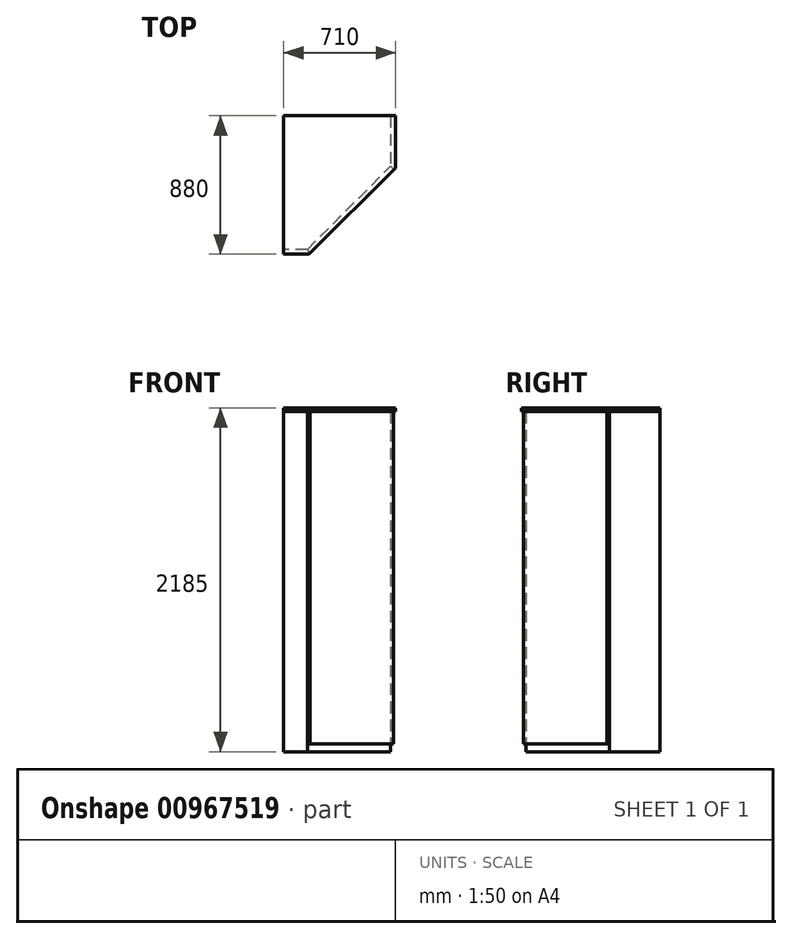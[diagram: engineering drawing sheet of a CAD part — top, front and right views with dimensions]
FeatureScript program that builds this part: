
annotation { "Feature Type Name" : "Feature", "Feature Type Description" : "" }
export const myFeature = defineFeature(function(context is Context, id is Id, definition is map)
    precondition{}
    {
        {
            assignVariable(context, id + "F0", {"variableType" : VariableType.LENGTH, "name" : "H", "lengthValue" : 2200 * mm});
        }
        {
            var Q0;
            Q0=qCreatedBy(makeId("Top.planeOp"),FACE);
            var sketch = newSketch(context, id + "F1", { "sketchPlane" : qUnion([Q0])});
            skLineSegment(sketch, "E0", {"start": v(0, 0) * mm, "end": v(680, 0) * mm});
            skLineSegment(sketch, "E1", {"start": v(680, 0) * mm, "end": v(680, -320) * mm});
            skLineSegment(sketch, "E2", {"start": v(680, -320) * mm, "end": v(150, -850) * mm});
            skLineSegment(sketch, "E3", {"start": v(150, -850) * mm, "end": v(0, -850) * mm});
            skLineSegment(sketch, "E4", {"start": v(0, -850) * mm, "end": v(0, 0) * mm});
            skSolve(sketch);
        }
        {
            var Q0;
            Q0 = qSketchRegion(id + "F1", true);
            extrude(context, id + "F2", {"entities" : qUnion([Q0]), "depth" : getVariable(context, 'H') - 40 * mm, "offsetDistance" : 25 * mm});
        }
        {
            var Q0;
            Q0=makeQuery(id+"F2.opExtrude","SWEPT_FACE",FACE,{"disambiguationData":[OSD([sQuery(id+"F1.wireOp",EDGE,"E2")])]});
            var sketch = newSketch(context, id + "F3", { "sketchPlane" : qUnion([Q0])});
            skLineSegment(sketch, "E5.bottom", {"start": v(-494.97, 2160) * mm, "end": v(254.56, 2160) * mm});
            skLineSegment(sketch, "E5.top", {"start": v(-494.97, 50) * mm, "end": v(254.56, 50) * mm});
            skLineSegment(sketch, "E5.left", {"start": v(-494.97, 2160) * mm, "end": v(-494.97, 50) * mm});
            skLineSegment(sketch, "E5.right", {"start": v(254.56, 2160) * mm, "end": v(254.56, 50) * mm});
            skSolve(sketch);
        }
        {
            var Q0;
            Q0 = qSketchRegion(id + "F3", true);
            extrude(context, id + "F4", {"entities" : qUnion([Q0]), "depth" : 25 * mm, "offsetDistance" : 25 * mm});
        }
        {
            var Q0;
            Q0=makeQuery(id+"F2.opExtrude","CAP_FACE",FACE,{"disambiguationData":[OSD([sQuery(id+"F1.wireOp",EDGE,"E0"),sQuery(id+"F1.wireOp",EDGE,"E1"),sQuery(id+"F1.wireOp",EDGE,"E2"),sQuery(id+"F1.wireOp",EDGE,"E3"),sQuery(id+"F1.wireOp",EDGE,"E4")])],"isStart":false});
            var sketch = newSketch(context, id + "F5", { "sketchPlane" : qUnion([Q0])});
            skLineSegment(sketch, "E6.0.2", {"start": v(0, -850) * mm, "end": v(150, -850) * mm, "construction": true});
            skLineSegment(sketch, "E6.0.3", {"start": v(150, -850) * mm, "end": v(680, -320) * mm, "construction": true});
            skLineSegment(sketch, "E6.0.4", {"start": v(680, -320) * mm, "end": v(680, 0) * mm, "construction": true});
            skLineSegment(sketch, "E7.0", {"start": v(710, -332.43) * mm, "end": v(710, 0) * mm});
            skLineSegment(sketch, "E7.1", {"start": v(162.43, -880) * mm, "end": v(710, -332.43) * mm});
            skLineSegment(sketch, "E7.2", {"start": v(0, -880) * mm, "end": v(162.43, -880) * mm});
            skLineSegment(sketch, "E8", {"start": v(0, -880) * mm, "end": v(0, 0) * mm});
            skLineSegment(sketch, "E9", {"start": v(710, 0) * mm, "end": v(0, 0) * mm});
            skSolve(sketch);
        }
        {
            var Q0;
            Q0 = qSketchRegion(id + "F5", true);
            extrude(context, id + "F6", {"entities" : qUnion([Q0]), "depth" : 25 * mm, "hasOffset" : true, "offsetDistance" : 20 * mm, "offsetOppositeDirection" : true});
        }
    });
